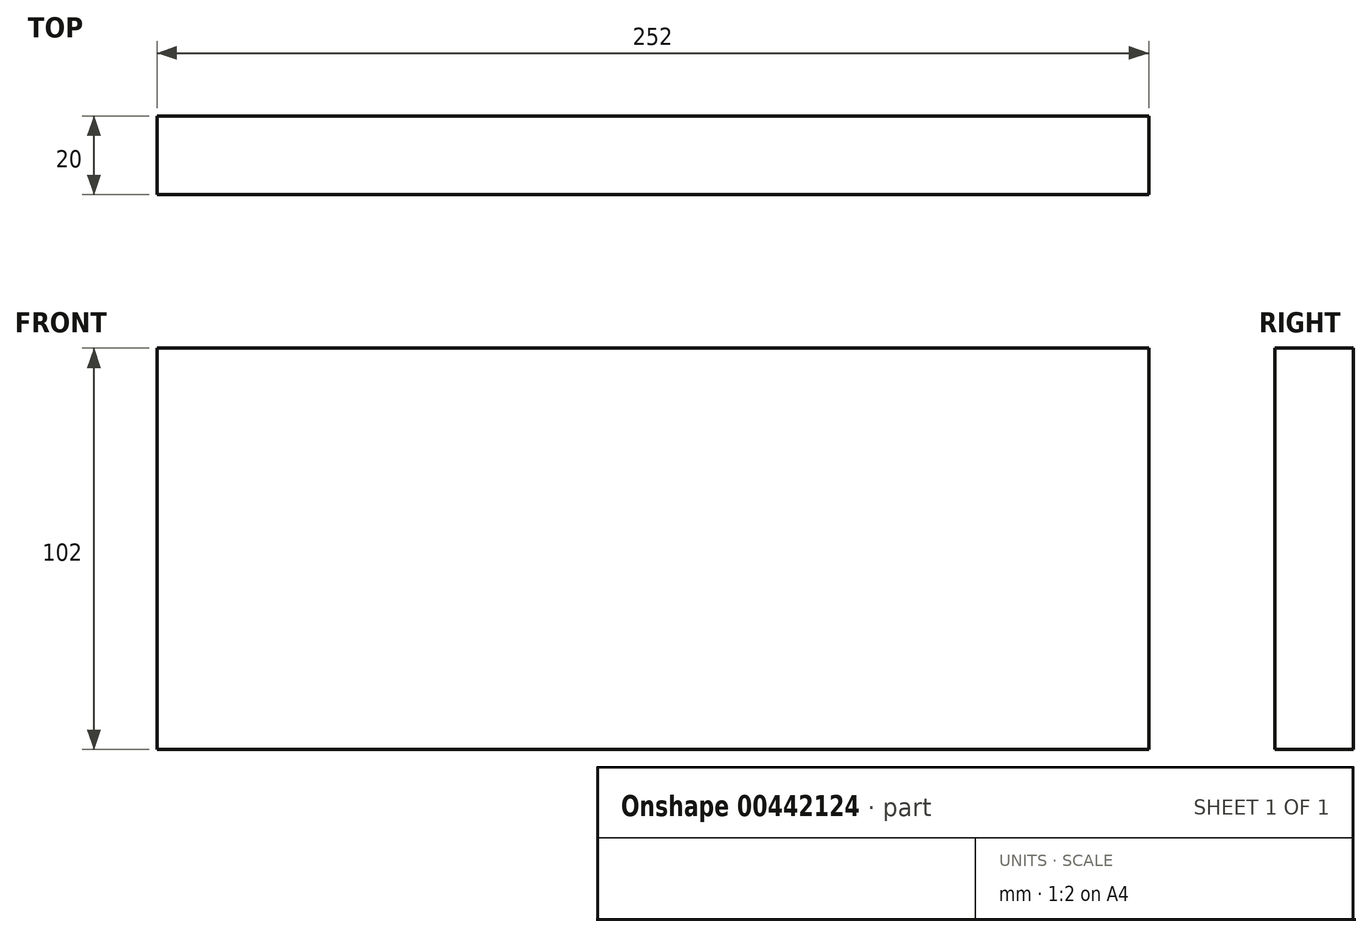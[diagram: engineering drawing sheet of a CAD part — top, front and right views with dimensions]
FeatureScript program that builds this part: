
annotation { "Feature Type Name" : "Feature", "Feature Type Description" : "" }
export const myFeature = defineFeature(function(context is Context, id is Id, definition is map)
    precondition{}
    {
        {
            var Q0;
            Q0=qCreatedBy(makeId("Top.planeOp"),FACE);
            var sketch = newSketch(context, id + "F0", { "sketchPlane" : qUnion([Q0])});
            skLineSegment(sketch, "E0.bottom", {"start": v(-126, 10) * mm, "end": v(126, 10) * mm});
            skLineSegment(sketch, "E0.top", {"start": v(-126, -10) * mm, "end": v(126, -10) * mm});
            skLineSegment(sketch, "E0.left", {"start": v(-126, 10) * mm, "end": v(-126, -10) * mm});
            skLineSegment(sketch, "E0.right", {"start": v(126, 10) * mm, "end": v(126, -10) * mm});
            skPoint(sketch, "E0.middle", {"position": v(0, 0) * mm});
            skSolve(sketch);
        }
        {
            var Q0;
            Q0=makeQuery(id+"F0.imprint","IMPRINT",FACE,{"disambiguationData":[TD([[makeQuery(id+"F0.imprint","IMPRINT",EDGE,{"derivedFrom":sQuery(id+"F0.wireOp",EDGE,"E0.bottom")}),-1.0]])]});
            extrude(context, id + "F1", {"entities" : qUnion([Q0]), "depth" : 102 * mm});
        }
    });
